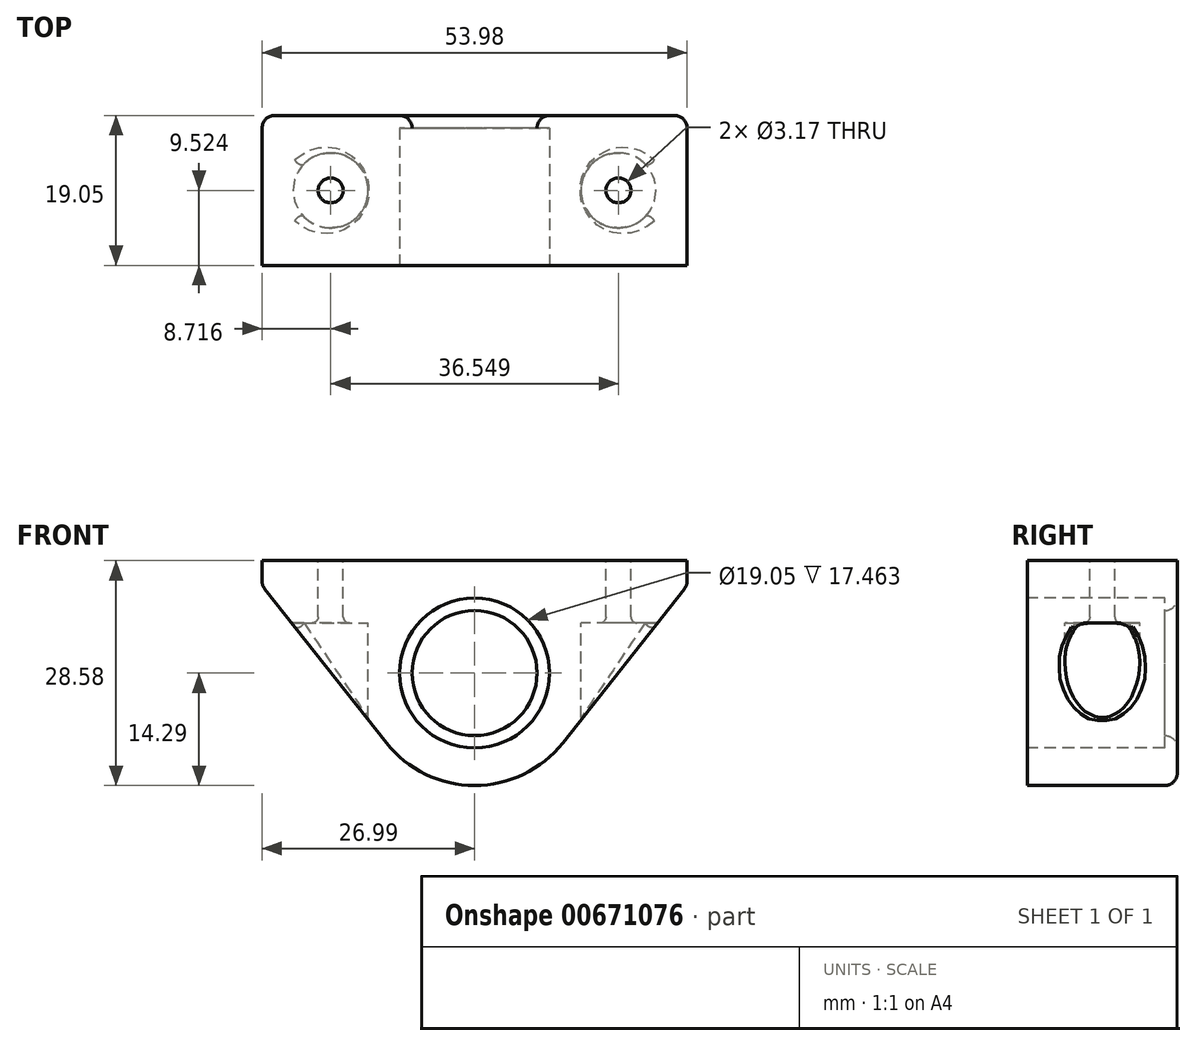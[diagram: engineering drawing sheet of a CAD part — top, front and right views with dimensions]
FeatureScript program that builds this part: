
annotation { "Feature Type Name" : "Feature", "Feature Type Description" : "" }
export const myFeature = defineFeature(function(context is Context, id is Id, definition is map)
    precondition{}
    {
        {
            var Q0;
            Q0=qCreatedBy(makeId("Front.planeOp"),FACE);
            var sketch = newSketch(context, id + "F0", { "sketchPlane" : qUnion([Q0])});
            skCircle(sketch, "E0", {"center": v(0, 0) * mm, "radius": 14.29 * mm});
            skCircle(sketch, "E1", {"center": v(0, 0) * mm, "radius": 7.94 * mm});
            skLineSegment(sketch, "E2", {"start": v(-11.21, -8.86) * mm, "end": v(-26.99, 11.11) * mm});
            skLineSegment(sketch, "E3", {"start": v(-26.99, 11.11) * mm, "end": v(26.99, 11.11) * mm});
            skLineSegment(sketch, "E4", {"start": v(26.99, 11.11) * mm, "end": v(11.21, -8.86) * mm});
            skLineSegment(sketch, "E5", {"start": v(0, 0) * mm, "end": v(0, 22.65) * mm, "construction": true});
            skLineSegment(sketch, "E6.top", {"start": v(-26.99, 14.29) * mm, "end": v(26.99, 14.29) * mm});
            skLineSegment(sketch, "E6.left", {"start": v(-26.99, 11.11) * mm, "end": v(-26.99, 14.29) * mm});
            skLineSegment(sketch, "E6.right", {"start": v(26.99, 11.11) * mm, "end": v(26.99, 14.29) * mm});
            skSolve(sketch);
        }
        {
            var Q0;
            Q0 = qSketchRegion(id + "F0", true);
            extrude(context, id + "F1", {"entities" : qUnion([Q0]), "depth" : 19.05 * mm, "offsetDistance" : 25.4 * mm});
        }
        {
            var Q0;
            Q0=makeQuery(id+"F1.opExtrude","CAP_FACE",FACE,{"disambiguationData":[OSD([sQuery(id+"F0.wireOp",EDGE,"E0"),sQuery(id+"F0.wireOp",EDGE,"E1"),sQuery(id+"F0.wireOp",EDGE,"E2"),sQuery(id+"F0.wireOp",EDGE,"E4"),sQuery(id+"F0.wireOp",EDGE,"E6.top"),sQuery(id+"F0.wireOp",EDGE,"E6.left"),sQuery(id+"F0.wireOp",EDGE,"E6.right")])],"isStart":false});
            var sketch = newSketch(context, id + "F2", { "sketchPlane" : qUnion([Q0])});
            skCircle(sketch, "E7", {"center": v(0, 0) * mm, "radius": 9.53 * mm});
            skCircle(sketch, "E8.0", {"center": v(0, 0) * mm, "radius": 7.94 * mm, "construction": true});
            skSolve(sketch);
        }
        {
            var Q0;
            Q0 = qSketchRegion(id + "F2", true);
            extrude(context, id + "F3", {"entities" : qUnion([Q0]), "operationType" : NewBodyOperationType.REMOVE, "oppositeDirection" : true, "depth" : 17.46 * mm, "offsetDistance" : 25.4 * mm});
        }
        {
            var Q0;
            Q0=makeQuery(id+"F1.opExtrude","CAP_EDGE",EDGE,{"disambiguationData":[OSD([sQuery(id+"F0.wireOp",EDGE,"E4")])],"isStart":true});
            var Q1;
            Q1=makeQuery(id+"F1.opExtrude","SWEPT_EDGE",EDGE,{"disambiguationData":[OSD([sQuery(id+"F0.wireOp",EDGE,"E4"),sQuery(id+"F0.wireOp",EDGE,"E3"),sQuery(id+"F0.wireOp",EDGE,"E6.right")])]});
            var Q2;
            Q2=makeQuery(id+"F1.opExtrude","SWEPT_EDGE",EDGE,{"disambiguationData":[OSD([sQuery(id+"F0.wireOp",EDGE,"E2"),sQuery(id+"F0.wireOp",EDGE,"E3"),sQuery(id+"F0.wireOp",EDGE,"E6.left")])]});
            var Q3;
            Q3=makeQuery(id+"F1.opExtrude","CAP_EDGE",EDGE,{"disambiguationData":[OSD([sQuery(id+"F0.wireOp",EDGE,"E6.left")])],"isStart":true});
            var Q4;
            Q4=makeQuery(id+"F1.opExtrude","CAP_EDGE",EDGE,{"disambiguationData":[OSD([sQuery(id+"F0.wireOp",EDGE,"E6.right")])],"isStart":true});
            var Q5;
            Q5=makeQuery(id+"F1.opExtrude","CAP_EDGE",EDGE,{"disambiguationData":[OSD([sQuery(id+"F0.wireOp",EDGE,"E1")])],"isStart":true});
            fillet(context, id + "F4", {"entities" : qUnion([Q0, Q1, Q2, Q3, Q4, Q5]), "radius" : 1.59 * mm, "tangentPropagation" : true, "allowEdgeOverflow" : false});
        }
        {
            var Q0;
            Q0=makeQuery(id+"F1.opExtrude","SWEPT_FACE",FACE,{"disambiguationData":[OSD([sQuery(id+"F0.wireOp",EDGE,"E6.top")])]});
            var sketch = newSketch(context, id + "F5", { "sketchPlane" : qUnion([Q0])});
            skLineSegment(sketch, "E9", {"start": v(-9.53, -17.46) * mm, "end": v(-9.53, -1.59) * mm, "construction": true});
            skLineSegment(sketch, "E10", {"start": v(9.53, -1.59) * mm, "end": v(9.53, -17.46) * mm, "construction": true});
            skCircle(sketch, "E11", {"center": v(-18.27, -9.53) * mm, "radius": 1.59 * mm});
            skLineSegment(sketch, "E12", {"start": v(-26.99, -10.32) * mm, "end": v(-18.27, -9.53) * mm, "construction": true});
            skLineSegment(sketch, "E13", {"start": v(-9.52, -9.53) * mm, "end": v(-18.27, -9.53) * mm, "construction": true});
            skCircle(sketch, "E14.MirrorC", {"center": v(18.27, -9.53) * mm, "radius": 1.59 * mm});
            skSolve(sketch);
        }
        {
            var Q0;
            Q0 = qSketchRegion(id + "F5", true);
            extrude(context, id + "F6", {"entities" : qUnion([Q0]), "operationType" : NewBodyOperationType.REMOVE, "endBound" : BoundingType.THROUGH_ALL, "oppositeDirection" : true, "depth" : 25.4 * mm, "offsetDistance" : 25.4 * mm});
        }
        {
            var Q0;
            Q0=qCreatedBy(makeId("Top.planeOp"),FACE);
            var sketch = newSketch(context, id + "F7", { "sketchPlane" : qUnion([Q0])});
            skCircle(sketch, "E15.0", {"center": v(18.27, -9.53) * mm, "radius": 1.59 * mm, "construction": true});
            skCircle(sketch, "E16", {"center": v(18.27, -9.53) * mm, "radius": 4.76 * mm});
            skCircle(sketch, "E17.MirrorC", {"center": v(-18.27, -9.53) * mm, "radius": 4.76 * mm});
            skSolve(sketch);
        }
        {
            var Q0;
            Q0 = qSketchRegion(id + "F7", true);
            extrude(context, id + "F8", {"entities" : qUnion([Q0]), "operationType" : NewBodyOperationType.REMOVE, "endBound" : BoundingType.THROUGH_ALL, "oppositeDirection" : true, "depth" : 25.4 * mm, "offsetDistance" : 25.4 * mm, "hasSecondDirection" : true, "secondDirectionOppositeDirection" : false, "secondDirectionDepth" : 6.35 * mm});
        }
        {
            var Q0;
            Q0=makeQuery(id+"F8.boolean.opBoolean","INTERSECT",EDGE,{"derivedFrom":[makeQuery(id+"F1.opExtrude","SWEPT_FACE",FACE,{"disambiguationData":[OSD([sQuery(id+"F0.wireOp",EDGE,"E2")])]}),makeQuery(id+"F8.opExtrude","SWEPT_FACE",FACE,{"disambiguationData":[OSD([sQuery(id+"F7.wireOp",EDGE,"E17.MirrorC")])]})]});
            var Q1;
            Q1=makeQuery(id+"F8.boolean.opBoolean","INTERSECT",EDGE,{"derivedFrom":[makeQuery(id+"F1.opExtrude","SWEPT_FACE",FACE,{"disambiguationData":[OSD([sQuery(id+"F0.wireOp",EDGE,"E4")])]}),makeQuery(id+"F8.opExtrude","SWEPT_FACE",FACE,{"disambiguationData":[OSD([sQuery(id+"F7.wireOp",EDGE,"E16")])]})]});
            var Q2;
            Q2=makeQuery(id+"F6.boolean.opBoolean","COPY",EDGE,{"derivedFrom":makeQuery(id+"F6.opExtrude","CAP_EDGE",EDGE,{"disambiguationData":[OSD([sQuery(id+"F5.wireOp",EDGE,"E11")])],"isStart":true})});
            var Q3;
            Q3=makeQuery(id+"F6.boolean.opBoolean","COPY",EDGE,{"derivedFrom":makeQuery(id+"F6.opExtrude","CAP_EDGE",EDGE,{"disambiguationData":[OSD([sQuery(id+"F5.wireOp",EDGE,"E14.MirrorC")])],"isStart":true})});
            var Q4;
            Q4=makeQuery(id+"F8.boolean.opBoolean","INTERSECT",EDGE,{"derivedFrom":[makeQuery(id+"F6.boolean.opBoolean","COPY",FACE,{"derivedFrom":makeQuery(id+"F6.opExtrude","SWEPT_FACE",FACE,{"disambiguationData":[OSD([sQuery(id+"F5.wireOp",EDGE,"E11")])]})}),makeQuery(id+"F8.opExtrude","CAP_FACE",FACE,{"disambiguationData":[OSD([sQuery(id+"F7.wireOp",EDGE,"E17.MirrorC")])],"isStart":true})]});
            var Q5;
            Q5=makeQuery(id+"F8.boolean.opBoolean","INTERSECT",EDGE,{"derivedFrom":[makeQuery(id+"F6.boolean.opBoolean","COPY",FACE,{"derivedFrom":makeQuery(id+"F6.opExtrude","SWEPT_FACE",FACE,{"disambiguationData":[OSD([sQuery(id+"F5.wireOp",EDGE,"E14.MirrorC")])]})}),makeQuery(id+"F8.opExtrude","CAP_FACE",FACE,{"disambiguationData":[OSD([sQuery(id+"F7.wireOp",EDGE,"E16")])],"isStart":true})]});
            var Q6;
            Q6=makeQuery(id+"F3.boolean.opBoolean","COPY",EDGE,{"derivedFrom":makeQuery(id+"F3.opExtrude","CAP_EDGE",EDGE,{"disambiguationData":[OSD([sQuery(id+"F2.wireOp",EDGE,"E7")])],"isStart":true})});
            fillet(context, id + "F9", {"entities" : qUnion([Q0, Q1, Q2, Q3, Q4, Q5, Q6]), "radius" : 0.8 * mm, "tangentPropagation" : true, "allowEdgeOverflow" : false});
        }
    });
